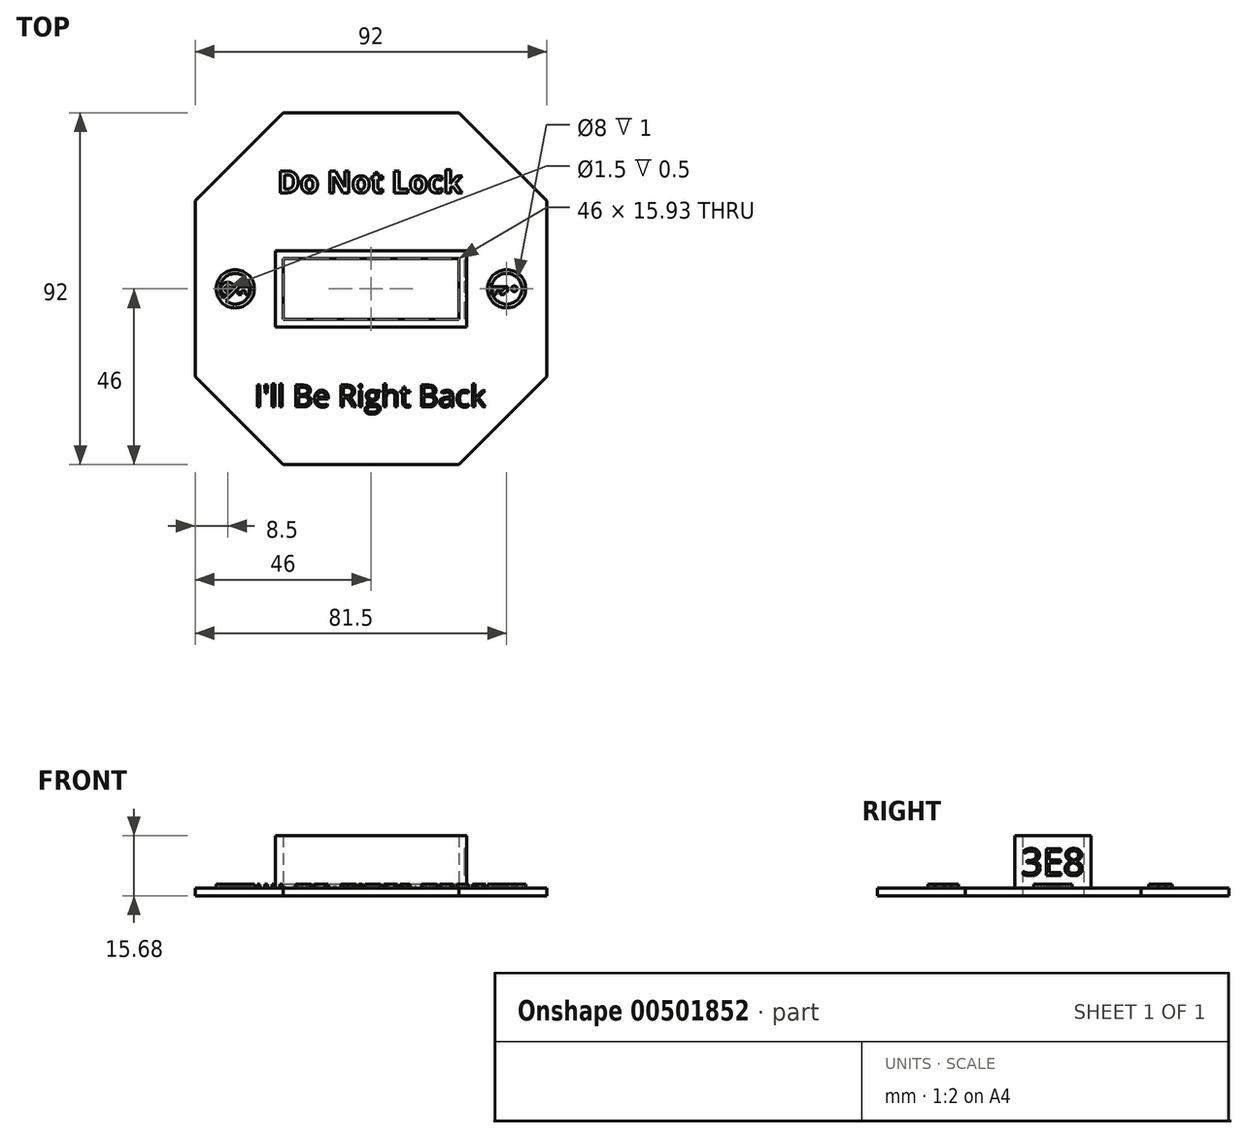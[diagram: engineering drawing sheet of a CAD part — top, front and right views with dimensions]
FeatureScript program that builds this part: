
annotation { "Feature Type Name" : "Feature", "Feature Type Description" : "" }
export const myFeature = defineFeature(function(context is Context, id is Id, definition is map)
    precondition{}
    {
        {
            assignVariable(context, id + "F0", {"name" : "latchlength", "anyValue" : 46});
        }
        {
            assignVariable(context, id + "F1", {"name" : "wallthick", "anyValue" : 2});
        }
        {
            assignVariable(context, id + "F2", {"name" : "textdepth", "anyValue" : 1});
        }
        {
            var Q0;
            Q0=qCreatedBy(makeId("Top.planeOp"),FACE);
            var sketch = newSketch(context, id + "F3", { "sketchPlane" : qUnion([Q0])});
            skLineSegment(sketch, "E0.bottom", {"start": v(23, -7.96) * mm, "end": v(-23, -7.96) * mm});
            skLineSegment(sketch, "E0.top", {"start": v(23, 7.97) * mm, "end": v(-23, 7.97) * mm});
            skLineSegment(sketch, "E0.left", {"start": v(23, -7.96) * mm, "end": v(23, 7.97) * mm});
            skLineSegment(sketch, "E0.right", {"start": v(-23, -7.96) * mm, "end": v(-23, 7.97) * mm});
            skPoint(sketch, "E0.middle", {"position": v(0, 0) * mm});
            skLineSegment(sketch, "E1.bottom", {"start": v(46, -46) * mm, "end": v(-46, -46) * mm});
            skLineSegment(sketch, "E1.top", {"start": v(46, 46) * mm, "end": v(-46, 46) * mm});
            skLineSegment(sketch, "E1.left", {"start": v(46, -46) * mm, "end": v(46, 46) * mm});
            skLineSegment(sketch, "E1.right", {"start": v(-46, -46) * mm, "end": v(-46, 46) * mm});
            skSolve(sketch);
        }
        {
            var Q0;
            Q0 = qSketchRegion(id + "F3", true);
            extrude(context, id + "F4", {"entities" : qUnion([Q0]), "depth" : (getVariable(context, 'wallthick')) * mm});
        }
        {
            var Q0;
            Q0=makeQuery(id+"F4.opExtrude","CAP_FACE",FACE,{"disambiguationData":[OSD([sQuery(id+"F3.wireOp",EDGE,"E0.bottom"),sQuery(id+"F3.wireOp",EDGE,"E0.top"),sQuery(id+"F3.wireOp",EDGE,"E0.left"),sQuery(id+"F3.wireOp",EDGE,"E0.right"),sQuery(id+"F3.wireOp",EDGE,"E1.bottom"),sQuery(id+"F3.wireOp",EDGE,"E1.top"),sQuery(id+"F3.wireOp",EDGE,"E1.left"),sQuery(id+"F3.wireOp",EDGE,"E1.right")])],"isStart":false});
            var sketch = newSketch(context, id + "F5", { "sketchPlane" : qUnion([Q0])});
            skLineSegment(sketch, "E2.0", {"start": v(23, 7.97) * mm, "end": v(-23, 7.97) * mm});
            skLineSegment(sketch, "E3.0", {"start": v(-23, -7.96) * mm, "end": v(-23, 7.97) * mm});
            skLineSegment(sketch, "E4.0", {"start": v(23, -7.96) * mm, "end": v(23, 7.97) * mm});
            skLineSegment(sketch, "E5.0", {"start": v(23, -7.96) * mm, "end": v(-23, -7.96) * mm});
            skLineSegment(sketch, "E6.0", {"start": v(25, 9.97) * mm, "end": v(-25, 9.97) * mm});
            skLineSegment(sketch, "E6.1", {"start": v(25, -9.96) * mm, "end": v(25, 9.97) * mm});
            skLineSegment(sketch, "E6.2", {"start": v(25, -9.96) * mm, "end": v(-25, -9.97) * mm});
            skLineSegment(sketch, "E6.3", {"start": v(-25, -9.97) * mm, "end": v(-25, 9.97) * mm});
            skSolve(sketch);
        }
        {
            var Q0;
            Q0 = qSketchRegion(id + "F5", true);
            extrude(context, id + "F6", {"entities" : qUnion([Q0]), "operationType" : NewBodyOperationType.ADD, "depth" : 13.68 * mm});
        }
        {
            var Q0;
            Q0=makeQuery(id+"F4.opExtrude","CAP_FACE",FACE,{"disambiguationData":[OSD([sQuery(id+"F3.wireOp",EDGE,"E0.bottom"),sQuery(id+"F3.wireOp",EDGE,"E0.top"),sQuery(id+"F3.wireOp",EDGE,"E0.left"),sQuery(id+"F3.wireOp",EDGE,"E0.right"),sQuery(id+"F3.wireOp",EDGE,"E1.bottom"),sQuery(id+"F3.wireOp",EDGE,"E1.top"),sQuery(id+"F3.wireOp",EDGE,"E1.left"),sQuery(id+"F3.wireOp",EDGE,"E1.right")])],"isStart":false});
            var sketch = newSketch(context, id + "F7", { "sketchPlane" : qUnion([Q0])});
            skText(sketch, "E7", { "text": "Do Not Lock", "fontName": "OpenSans-Bold.ttf"});
            skLineSegment(sketch, "E8", {"start": v(0, 46) * mm, "end": v(0, 9.97) * mm, "construction": true});
            skPoint(sketch, "E9", {"position": v(0, 27.98) * mm});
            skCircle(sketch, "E10", {"center": v(-35.5, 0) * mm, "radius": 5 * mm});
            skPoint(sketch, "E10.centerSnap0", {"position": v(-46, 0) * mm});
            skLineSegment(sketch, "E11", {"start": v(-46, 0) * mm, "end": v(-25, 0) * mm, "construction": true});
            skCircle(sketch, "E12", {"center": v(-37.5, 0) * mm, "radius": 1.75 * mm});
            skCircle(sketch, "E13", {"center": v(-37.5, 0) * mm, "radius": 0.75 * mm});
            skLineSegment(sketch, "E14", {"start": v(-35.82, 0.5) * mm, "end": v(-31.82, 0.5) * mm});
            skLineSegment(sketch, "E15", {"start": v(-31.82, 0.5) * mm, "end": v(-31.82, -1.5) * mm});
            skLineSegment(sketch, "E16", {"start": v(-31.82, -1.5) * mm, "end": v(-32.82, -1.5) * mm});
            skLineSegment(sketch, "E17", {"start": v(-32.82, -1.5) * mm, "end": v(-32.82, -0.5) * mm});
            skLineSegment(sketch, "E18", {"start": v(-32.82, -0.5) * mm, "end": v(-33.82, -0.5) * mm});
            skLineSegment(sketch, "E19", {"start": v(-33.82, -0.5) * mm, "end": v(-33.82, -1.5) * mm});
            skLineSegment(sketch, "E20", {"start": v(-33.82, -1.5) * mm, "end": v(-34.82, -1.5) * mm});
            skLineSegment(sketch, "E21", {"start": v(-34.82, -1.5) * mm, "end": v(-34.82, -0.5) * mm});
            skLineSegment(sketch, "E22", {"start": v(-34.82, -0.5) * mm, "end": v(-35.82, -0.5) * mm});
            skCircle(sketch, "E23", {"center": v(-35.5, 0) * mm, "radius": 4 * mm});
            skLineSegment(sketch, "E24", {"start": v(-33.05, 3.16) * mm, "end": v(-38.66, -2.45) * mm});
            skLineSegment(sketch, "E25", {"start": v(-32.34, 2.45) * mm, "end": v(-37.95, -3.16) * mm});
            skLineSegment(sketch, "E26", {"start": v(-35.85, 0.35) * mm, "end": v(-35.5, 0) * mm, "construction": true});
            skLineSegment(sketch, "E27", {"start": v(-35.5, 0) * mm, "end": v(-35.15, -0.35) * mm, "construction": true});
            skLineSegment(sketch, "E28", {"start": v(-21.29, 0.5) * mm, "end": v(-21.29, 0) * mm, "construction": true});
            skCircle(sketch, "E29.MirrorC", {"center": v(35.5, 0) * mm, "radius": 5 * mm});
            skCircle(sketch, "E30.MirrorC", {"center": v(35.5, 0) * mm, "radius": 4 * mm});
            skLineSegment(sketch, "E31.MirrorCS", {"start": v(31.82, 0.5) * mm, "end": v(31.82, -1.5) * mm});
            skLineSegment(sketch, "E32.MirrorCS", {"start": v(35.82, 0.5) * mm, "end": v(31.82, 0.5) * mm});
            skLineSegment(sketch, "E33.MirrorCS", {"start": v(32.82, -1.5) * mm, "end": v(32.82, -0.5) * mm});
            skLineSegment(sketch, "E34.MirrorCS", {"start": v(32.82, -0.5) * mm, "end": v(33.82, -0.5) * mm});
            skLineSegment(sketch, "E35.MirrorCS", {"start": v(33.82, -0.5) * mm, "end": v(33.82, -1.5) * mm});
            skLineSegment(sketch, "E36.MirrorCS", {"start": v(33.82, -1.5) * mm, "end": v(34.82, -1.5) * mm});
            skLineSegment(sketch, "E37.MirrorCS", {"start": v(34.82, -1.5) * mm, "end": v(34.82, -0.5) * mm});
            skLineSegment(sketch, "E38.MirrorCS", {"start": v(34.82, -0.5) * mm, "end": v(35.82, -0.5) * mm});
            skCircle(sketch, "E39.MirrorC", {"center": v(37.5, 0) * mm, "radius": 1.75 * mm});
            skCircle(sketch, "E40.MirrorC", {"center": v(37.5, 0) * mm, "radius": 0.75 * mm});
            skLineSegment(sketch, "E41.MirrorCS", {"start": v(31.82, -1.5) * mm, "end": v(32.82, -1.5) * mm});
            skLineSegment(sketch, "E42.MirrorCS", {"start": v(33.05, 3.16) * mm, "end": v(38.66, -2.45) * mm, "construction": true});
            skLineSegment(sketch, "E43.MirrorCS", {"start": v(32.34, 2.45) * mm, "end": v(37.95, -3.16) * mm, "construction": true});
            skLineSegment(sketch, "E44", {"start": v(35.5, 4) * mm, "end": v(35.5, -4) * mm, "construction": true});
            skLineSegment(sketch, "E45.MirrorCS", {"start": v(37.95, 3.16) * mm, "end": v(32.34, -2.45) * mm});
            skLineSegment(sketch, "E46.MirrorCS", {"start": v(38.66, 2.45) * mm, "end": v(33.05, -3.16) * mm});
            skLineSegment(sketch, "E47", {"start": v(0, -9.96) * mm, "end": v(0, -46) * mm, "construction": true});
            skText(sketch, "E48", { "text": "I\'ll Be Right Back", "fontName": "OpenSans-Regular.ttf"});
            skPoint(sketch, "E49", {"position": v(0, -27.98) * mm});
            const initialGuessF7  = {"E7": [-0.02447, 0.0251, 1, 0, 0.00575], "E48": [-0.0305, -0.03086, 1, 0, 0.00575]};
            skSetInitialGuess(sketch, initialGuessF7);
            skSolve(sketch);
        }
        {
            var Q0;
            Q0 = qSketchRegion(id + "F7", true);
            var Q1;
            {var subQ0=sQuery(id+"F7.wireOp",EDGE,"E24");var subQ1=sQuery(id+"F7.wireOp",EDGE,"E14");var subQ2=makeQuery(id+"F7.imprint","INTERSECT",VERTEX,{"derivedFrom":[subQ1,subQ0]});Q1=makeQuery(id+"F7.imprint","IMPRINT",FACE,{"disambiguationData":[TD([[makeQuery(id+"F7.imprint","IMPRINT",EDGE,{"disambiguationData":[TD([[subQ2,-1.0]])],"derivedFrom":subQ1}),1.0]])]});}
            var Q2;
            {var subQ1=sQuery(id+"F7.wireOp",EDGE,"E12");var subQ5=sQuery(id+"F7.wireOp",EDGE,"E22");var subQ6=makeQuery(id+"F7.imprint","INTERSECT",VERTEX,{"derivedFrom":[subQ1,subQ5]});Q2=makeQuery(id+"F7.imprint","IMPRINT",FACE,{"disambiguationData":[TD([[makeQuery(id+"F7.imprint","IMPRINT",EDGE,{"disambiguationData":[TD([[subQ6,-1.0]])],"derivedFrom":subQ1}),-1.0]])]});}
            var Q3;
            {var subQ0=sQuery(id+"F7.wireOp",EDGE,"E12");var subQ1=makeQuery(id+"F7.imprint","INTERSECT",VERTEX,{"derivedFrom":[subQ0,sQuery(id+"F7.wireOp",EDGE,"E22")]});Q3=makeQuery(id+"F7.imprint","IMPRINT",FACE,{"disambiguationData":[TD([[makeQuery(id+"F7.imprint","IMPRINT",EDGE,{"disambiguationData":[TD([[subQ1,1.0]])],"derivedFrom":subQ0}),1.0]])]});}
            var Q4;
            {var subQ3=sQuery(id+"F7.wireOp",EDGE,"E12");var subQ5=sQuery(id+"F7.wireOp",EDGE,"E22");var subQ6=makeQuery(id+"F7.imprint","INTERSECT",VERTEX,{"derivedFrom":[subQ3,subQ5]});Q4=makeQuery(id+"F7.imprint","IMPRINT",FACE,{"disambiguationData":[TD([[makeQuery(id+"F7.imprint","IMPRINT",EDGE,{"disambiguationData":[TD([[subQ6,1.0]])],"derivedFrom":subQ3}),-1.0]])]});}
            var Q5;
            {var subQ0=sQuery(id+"F7.wireOp",EDGE,"E45.MirrorCS");var subQ1=sQuery(id+"F7.wireOp",EDGE,"E30.MirrorC");var subQ2=makeQuery(id+"F7.imprint","INTERSECT",VERTEX,{"disambiguationData":[OD(0.0)],"derivedFrom":[subQ1,subQ0]});Q5=makeQuery(id+"F7.imprint","IMPRINT",FACE,{"disambiguationData":[TD([[makeQuery(id+"F7.imprint","IMPRINT",EDGE,{"disambiguationData":[TD([[subQ2,-1.0]])],"derivedFrom":subQ1}),-1.0]])]});}
            var Q6;
            {var subQ0=sQuery(id+"F7.wireOp",EDGE,"E39.MirrorC");var subQ1=makeQuery(id+"F7.imprint","INTERSECT",VERTEX,{"derivedFrom":[sQuery(id+"F7.wireOp",EDGE,"E32.MirrorCS"),subQ0]});Q6=makeQuery(id+"F7.imprint","IMPRINT",FACE,{"disambiguationData":[TD([[makeQuery(id+"F7.imprint","IMPRINT",EDGE,{"disambiguationData":[TD([[subQ1,-1.0]])],"derivedFrom":subQ0}),-1.0]])]});}
            var Q7;
            {var subQ11=sQuery(id+"F7.wireOp",EDGE,"E39.MirrorC");var subQ12=sQuery(id+"F7.wireOp",EDGE,"E32.MirrorCS");var subQ13=makeQuery(id+"F7.imprint","INTERSECT",VERTEX,{"derivedFrom":[subQ12,subQ11]});Q7=makeQuery(id+"F7.imprint","IMPRINT",FACE,{"disambiguationData":[TD([[makeQuery(id+"F7.imprint","IMPRINT",EDGE,{"disambiguationData":[TD([[subQ13,-1.0]])],"derivedFrom":subQ12}),1.0]])]});}
            var Q8;
            {var subQ0=sQuery(id+"F7.wireOp",EDGE,"E38.MirrorCS");var subQ1=sQuery(id+"F7.wireOp",EDGE,"E37.MirrorCS");var subQ2=makeQuery(id+"F7.imprint","INTERSECT",VERTEX,{"derivedFrom":[subQ1,subQ0]});Q8=makeQuery(id+"F7.imprint","IMPRINT",FACE,{"disambiguationData":[TD([[makeQuery(id+"F7.imprint","IMPRINT",EDGE,{"disambiguationData":[TD([[subQ2,1.0]])],"derivedFrom":subQ1}),-1.0]])]});}
            var Q9;
            {var subQ5=sQuery(id+"F7.wireOp",EDGE,"E45.MirrorCS");var subQ6=sQuery(id+"F7.wireOp",EDGE,"E30.MirrorC");var subQ7=makeQuery(id+"F7.imprint","INTERSECT",VERTEX,{"disambiguationData":[OD(1.0)],"derivedFrom":[subQ6,subQ5]});Q9=makeQuery(id+"F7.imprint","IMPRINT",FACE,{"disambiguationData":[TD([[makeQuery(id+"F7.imprint","IMPRINT",EDGE,{"disambiguationData":[TD([[subQ7,1.0]])],"derivedFrom":subQ6}),-1.0]])]});}
            extrude(context, id + "F8", {"entities" : qUnion([Q0, Q1, Q2, Q3, Q4, Q5, Q6, Q7, Q8, Q9]), "operationType" : NewBodyOperationType.ADD, "depth" : (getVariable(context, 'textdepth')) * mm});
        }
        {
            var Q0;
            {var subQ12=sQuery(id+"F7.wireOp",EDGE,"E17");Q0=makeQuery(id+"F7.imprint","IMPRINT",FACE,{"disambiguationData":[TD([[makeQuery(id+"F7.imprint","IMPRINT",EDGE,{"derivedFrom":subQ12}),-1.0]])]});}
            var Q1;
            Q1=makeQuery(id+"F7.imprint","IMPRINT",FACE,{"disambiguationData":[TD([[makeQuery(id+"F7.imprint","IMPRINT",EDGE,{"derivedFrom":sQuery(id+"F7.wireOp",EDGE,"E13")}),-1.0]])]});
            var Q2;
            Q2=makeQuery(id+"F7.imprint","IMPRINT",FACE,{"disambiguationData":[TD([[makeQuery(id+"F7.imprint","IMPRINT",EDGE,{"derivedFrom":sQuery(id+"F7.wireOp",EDGE,"E40.MirrorC")}),1.0]])]});
            var Q3;
            {var subQ2=sQuery(id+"F7.wireOp",EDGE,"E31.MirrorCS");Q3=makeQuery(id+"F7.imprint","IMPRINT",FACE,{"disambiguationData":[TD([[makeQuery(id+"F7.imprint","IMPRINT",EDGE,{"derivedFrom":subQ2}),1.0]])]});}
            var Q4;
            {var subQ0=sQuery(id+"F7.wireOp",EDGE,"E37.MirrorCS");var subQ1=sQuery(id+"F7.wireOp",EDGE,"E36.MirrorCS");var subQ2=makeQuery(id+"F7.imprint","INTERSECT",VERTEX,{"derivedFrom":[subQ1,subQ0]});Q4=makeQuery(id+"F7.imprint","IMPRINT",FACE,{"disambiguationData":[TD([[makeQuery(id+"F7.imprint","IMPRINT",EDGE,{"disambiguationData":[TD([[subQ2,1.0]])],"derivedFrom":subQ1}),1.0]])]});}
            extrude(context, id + "F9", {"entities" : qUnion([Q0, Q1, Q2, Q3, Q4]), "operationType" : NewBodyOperationType.ADD, "depth" : (getVariable(context, 'textdepth') - .5) * mm});
        }
        {
            var Q0;
            Q0=makeQuery(id+"F4.opExtrude","SWEPT_EDGE",EDGE,{"disambiguationData":[OSD([sQuery(id+"F3.wireOp",EDGE,"E1.top"),sQuery(id+"F3.wireOp",EDGE,"E1.right")])]});
            var Q1;
            Q1=makeQuery(id+"F4.opExtrude","SWEPT_EDGE",EDGE,{"disambiguationData":[OSD([sQuery(id+"F3.wireOp",EDGE,"E1.bottom"),sQuery(id+"F3.wireOp",EDGE,"E1.right")])]});
            var Q2;
            Q2=makeQuery(id+"F4.opExtrude","SWEPT_EDGE",EDGE,{"disambiguationData":[OSD([sQuery(id+"F3.wireOp",EDGE,"E1.bottom"),sQuery(id+"F3.wireOp",EDGE,"E1.left")])]});
            var Q3;
            Q3=makeQuery(id+"F4.opExtrude","SWEPT_EDGE",EDGE,{"disambiguationData":[OSD([sQuery(id+"F3.wireOp",EDGE,"E1.top"),sQuery(id+"F3.wireOp",EDGE,"E1.left")])]});
            chamfer(context, id + "F10", {"entities" : qUnion([Q0, Q1, Q2, Q3]), "width" : (getVariable(context, 'latchlength') / 2) * mm, "tangentPropagation" : true});
        }
        {
            var Q0;
            Q0=makeQuery(id+"F6.opExtrude","SWEPT_FACE",FACE,{"disambiguationData":[OSD([sQuery(id+"F5.wireOp",EDGE,"E6.1")])]});
            var sketch = newSketch(context, id + "F11", { "sketchPlane" : qUnion([Q0])});
            skText(sketch, "E50", { "text": "3E8", "fontName": "OpenSans-Regular.ttf"});
            skPoint(sketch, "E51", {"position": v(0, 8.84) * mm});
            skLineSegment(sketch, "E52", {"start": v(-9.97, 15.68) * mm, "end": v(9.96, 2) * mm, "construction": true});
            const initialGuessF11  = {"E50": [-0.00833, 0.00534, 1, 0, 0.007]};
            skSetInitialGuess(sketch, initialGuessF11);
            skSolve(sketch);
        }
        {
            var Q0;
            Q0 = qSketchRegion(id + "F11", true);
            extrude(context, id + "F12", {"entities" : qUnion([Q0]), "operationType" : NewBodyOperationType.REMOVE, "oppositeDirection" : true, "depth" : .5 * mm});
        }
    });
